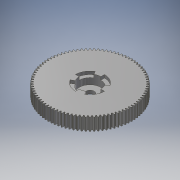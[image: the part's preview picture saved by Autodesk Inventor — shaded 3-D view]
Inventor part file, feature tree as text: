
AUTODESK INVENTOR PART (.ipt)
format: ipt  version: 2017 (Build 210142000, 142)  size: 535,040 bytes
history: native  units: mm (DEFAULTED — no unit token found)
features: sketch x5, extrude x4, plane x3, other x3, pattern_circular x1
ambient origin geometry x8: Origin, YZ Plane, XZ Plane, XY Plane, X Axis, Y Axis, Z Axis, Center Point
bodies: Solid1 (feature_tree)
feature tree (16):
  extrude  "Extrusion1"  Depth=20.0mm TaperAngle=0.0deg
  plane  "Work Plane2"
  plane  "Work Plane8"
  plane  "Work Plane9"
  other  "Spur Gear"
  extrude  "Extrusion2"  Depth=10.0mm TaperAngle=0.0deg
  extrude  "Extrusion3"  Depth=0.356999mm TaperAngle=0.0deg
  extrude  "Extrusion4"  TaperAngle=0.0deg  [1 undecoded]
  pattern_circular  "Circular Pattern1"  Count=8  [1 undecoded]
  sketch  "Sketch1"  dims[d0=136.0mm d1=20.0mm d2=0.0mm]
  sketch  "Sketch2"  dims[d3=132.830189mm d4=10.0mm d5=0.0mm]
  other  "Srf1"
  sketch  "Sketch3"  dims[d16=80.0mm d17=0.0mm d34=0.356999mm]
  sketch  "Sketch4"  dims[d39=0.0mm d41=0.0mm d43=80.0mm]
  sketch  "Sketch5"  dims[d46=80.0mm d47=0.0mm d48=0.0mm d49=9.525mm d50=10.0mm d51=0.0mm d52=35.0mm d53=15.0mm d54=0.0mm d55=6.0mm d56=60.0deg d57=5.0mm d58=0.0mm d59=40.0mm d60=360.0deg]
  other  "Pitch Diameter"
note: 2 required parameter values undecoded (feature->parameter linkage not recoverable at this tier; creation-order binding heuristic only, values carry confidence <= 0.55)
